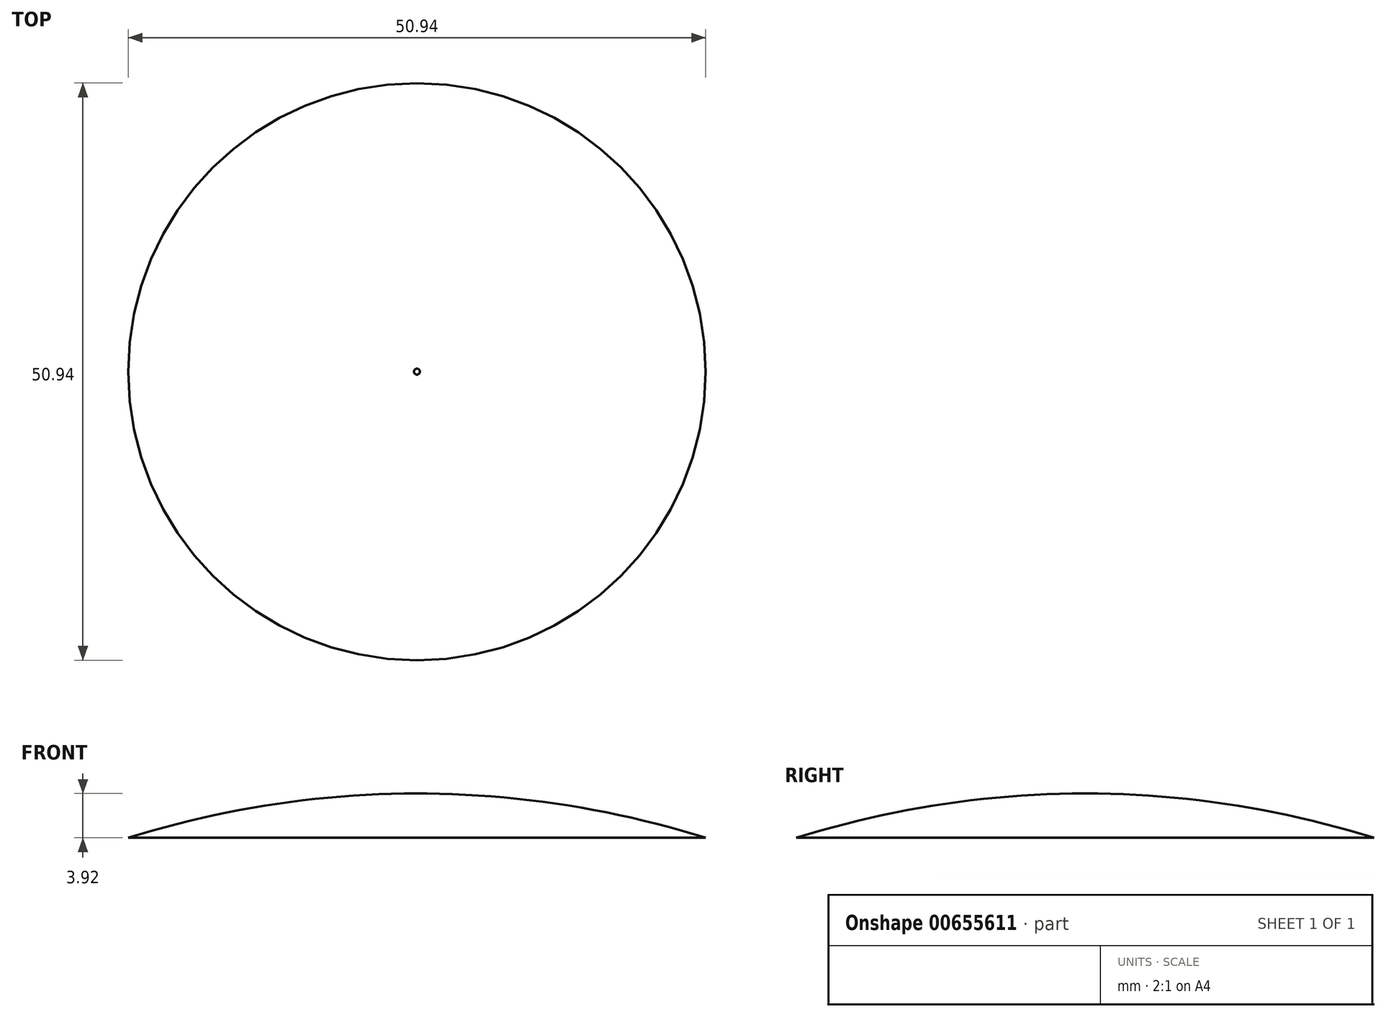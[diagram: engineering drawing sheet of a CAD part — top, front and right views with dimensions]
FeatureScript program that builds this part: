
annotation { "Feature Type Name" : "Feature", "Feature Type Description" : "" }
export const myFeature = defineFeature(function(context is Context, id is Id, definition is map)
    precondition{}
    {
        {
            var Q0;
            Q0=qCreatedBy(makeId("Front.planeOp"),FACE);
            var sketch = newSketch(context, id + "F0", { "sketchPlane" : qUnion([Q0])});
            skArc(sketch, "E0", {"start": v(25.47, 0) * mm, "mid": v(12.88, 2.92) * mm, "end": v(0, 3.92) * mm});
            skPoint(sketch, "E1", {"position": v(0, 3.92) * mm});
            skPoint(sketch, "E2.orphan", {"position": v(-25.73, 0) * mm});
            skLineSegment(sketch, "E3", {"start": v(0, 3.92) * mm, "end": v(0, 0) * mm});
            skLineSegment(sketch, "E4", {"start": v(25.47, 0) * mm, "end": v(0, 0) * mm});
            skLineSegment(sketch, "E5", {"start": v(0, -15.03) * mm, "end": v(0, 24.8) * mm});
            skSolve(sketch);
        }
        {
            var Q0;
            {var subQ0=sQuery(id+"F0.wireOp",EDGE,"E0");Q0=makeQuery(id+"F0.imprint","IMPRINT",FACE,{"disambiguationData":[TD([[makeQuery(id+"F0.imprint","IMPRINT",EDGE,{"derivedFrom":subQ0}),1.0]])]});}
            var Q1;
            Q1=sQuery(id+"F0.wireOp",EDGE,"E5");
            revolve(context, id + "F1", {"entities" : qUnion([Q0]), "axis" : qUnion([Q1]), "revolveType" : RevolveType.FULL});
        }
    });
